# Revit family: VL2xGL150xWSxxxB
name_source: partatom
category: Leuchten
units: mm (PartAtom-declared; Revit-internal decimal feet)

## family parameters
Basisbauteil = Fläche
Beim Laden mit Abzugskörper schneiden = Nein
Bemaßung runder Anschluss = Durchmesser verwenden
Gemeinsam genutzt = Nein
Lichtquelle = Ja
OmniClass-Nummer = 23.80.70.11
OmniClass-Titel = Luminaries for Internal Lighting
Raumberechnungspunkt = Nein
Teiletyp = Normal

## types (18) — shared parameters
Baugruppenkennzeichen = D5020200
Datei für fotometrisches Netz = Master_VLxx-GLxxxB_IP20.IES
Emissionsform beim Rendern sichtbar = Nein
Farbfilter = 16777215
Farbtemperaturverschiebung bei Dämpfen der Lampe = <Keine Auswahl>
Hersteller = RIDI Leuchten GmbH
Lampe = LED
Neigungswinkel = 90.00°
URL = www.ridi.de
Von Breite des Rechtecks ausssenden = 1480 mm  [stored 4.85564 ft]
Von Länge des Rechtecks aussenden = 61 mm  [stored 0.200131 ft]
brand = RIDI
conformity mark = CE
electrical safety class = 1
height = 64 mm  [stored 0.209974 ft]
ingress protection (IP) code = IP20
length = 1500 mm  [stored 4.92126 ft]
nominal frequency = 50-60Hz
nominal voltage = 230
voltage type (AC, DC, UC) = AC
weight = 1,7kg
width = 67 mm
zero-valued in all types: Vorgabe-Ansicht

## per-type parameters (varying)
| type | Modell | Scheinlast | product name | rated input power |
| VL2E-GL150-5FLWS840B0800 | 2550020
9 | 50 VA | VL2E-GL150-5FLWS840B0800 | 50 |
| VL2P-GL150-5FLWS840B1500 | 2550037 | 84 VA | VL2P-GL150-5FLWS840B1500 | 84 |
| VL2S-GL150-5FLWS865B0850 | 2550059 | 50 VA | VL2S-GL150-5FLWS865B0850 | 50 |
| VL2S-GL150-5FLWS840B0900 | 2550060 | 50 VA | VL2S-GL150-5FLWS840B0900 | 50 |
| VL2S-GL150-5FLWS840B1300 | 2550061 | 71 VA | VL2P-GL150-5FLWS850B1500 | 71 |
| VL2P-GL150-5FLWS850B1500 | 2550063 | 84 VA | VL2P-GL150-5FLWS850B1500 | 84 |
| VL2P-GL150-5FLWS865B1500 | 2550064 | 84 VA | VL2P-GL150-5FLWS865B1500 | 84 |
| VL2P-GL150-5FLWS840B0850 | 2550070 | 46 VA | VL2P-GL150-5FLWS840B0850 | 46 |
| VL2E-GL150-7DAWS840B0800 | 2560020 | 51 VA | VL2E-GL150-7DAWS840B0800 | 51 |
| VL2P-GL150-7DAWS840B1500 | 2560037 | 84 VA | VL2P-GL150-7DAWS840B1500 | 84 |
| VL2S-GL150-7DAWS840B0900 | 2560060 | 51 VA | VL2S-GL150-7DAWS840B0900 | 51 |
| VL2P-GL150-7DAWS865B1500 | 2560064 | 84 VA | VL2P-GL150-7DAWS865B1500 | 84 |
| VL2P-GL150-7DAWS840B0850 | 2560070 | 47 VA | VL2P-GL150-7DAWS840B0850 | 47 |
| VL2S-GL150-7DAWS840B1300 | 2560084 | 73 VA | VL2S-GL150-7DAWS840B1300 | 73 |
| VL2S-GL150-5FLWS865B1200 | 2550106 | 71 VA | VL2S-GL150-5FLWS865B1200 | 71 |
| VL2S-GL150-7DAWS865B0900 | 2560059 | 51 VA | VL2S-GL150-7DAWS865B0900 | 51 |
| VL2S-GL150-5FLWS850B0900 | 2550175 | 50 VA | VL2S-GL150-5FLWS850B0900 | 50 |
| VL2S-GL150-7DAWS850B0900 | 2560175 | 51 VA | VL2S-GL150-7DAWS850B0900 | 51 |

note: [stored X ft] marks values corroborated as IEEE doubles in the binary element streams (Revit-internal decimal feet)
